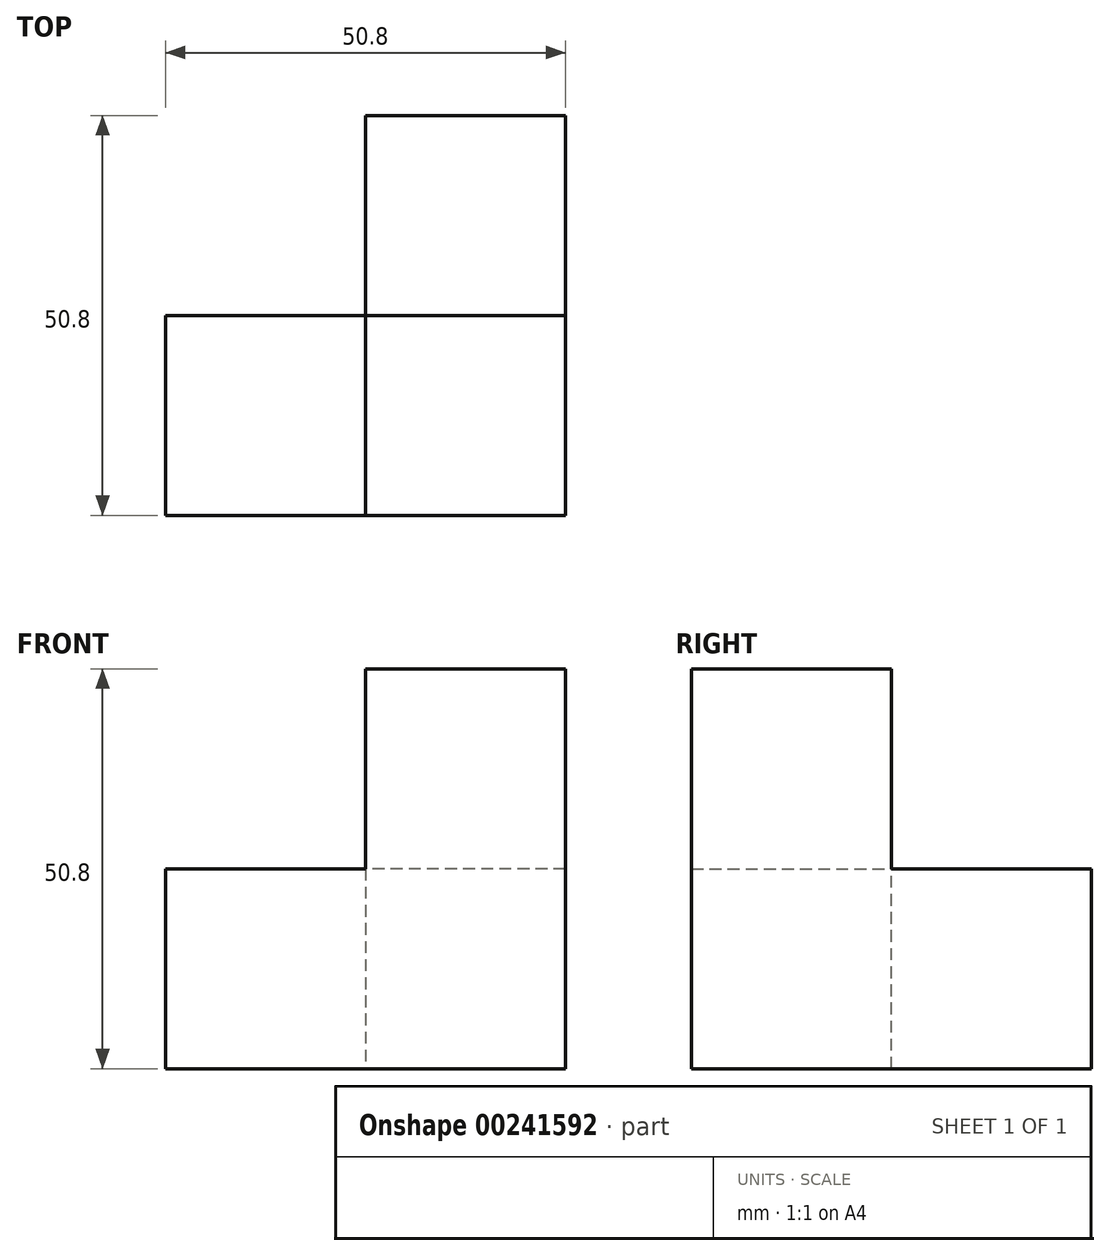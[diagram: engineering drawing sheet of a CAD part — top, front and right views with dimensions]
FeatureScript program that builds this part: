
annotation { "Feature Type Name" : "Feature", "Feature Type Description" : "" }
export const myFeature = defineFeature(function(context is Context, id is Id, definition is map)
    precondition{}
    {
        {
            var Q0;
            Q0=qCreatedBy(makeId("Front.planeOp"),FACE);
            var sketch = newSketch(context, id + "F0", { "sketchPlane" : qUnion([Q0])});
            skLineSegment(sketch, "E0.bottom", {"start": v(0, 0) * mm, "end": v(-25.4, 0) * mm});
            skLineSegment(sketch, "E0.top", {"start": v(0, 25.4) * mm, "end": v(-25.4, 25.4) * mm});
            skLineSegment(sketch, "E0.left", {"start": v(0, 0) * mm, "end": v(0, 25.4) * mm});
            skLineSegment(sketch, "E0.right", {"start": v(-25.4, 0) * mm, "end": v(-25.4, 25.4) * mm});
            skSolve(sketch);
        }
        {
            var Q0;
            Q0=makeQuery(id+"F0.imprint","IMPRINT",FACE,{"disambiguationData":[TD([[makeQuery(id+"F0.imprint","IMPRINT",EDGE,{"derivedFrom":sQuery(id+"F0.wireOp",EDGE,"E0.bottom")}),-1.0]])]});
            extrude(context, id + "F1", {"entities" : qUnion([Q0]), "depth" : 25.4 * mm});
        }
        {
            var Q0;
            Q0=makeQuery(id+"F1.opExtrude","SWEPT_FACE",FACE,{"disambiguationData":[OSD([sQuery(id+"F0.wireOp",EDGE,"E0.left")])]});
            var sketch = newSketch(context, id + "F2", { "sketchPlane" : qUnion([Q0])});
            skLineSegment(sketch, "E1.bottom", {"start": v(-25.4, 25.4) * mm, "end": v(0, 25.4) * mm});
            skLineSegment(sketch, "E1.top", {"start": v(-25.4, 0) * mm, "end": v(0, 0) * mm});
            skLineSegment(sketch, "E1.left", {"start": v(-25.4, 25.4) * mm, "end": v(-25.4, 0) * mm});
            skLineSegment(sketch, "E1.right", {"start": v(0, 25.4) * mm, "end": v(0, 0) * mm});
            skSolve(sketch);
        }
        {
            var Q0;
            Q0=makeQuery(id+"F2.imprint","IMPRINT",FACE,{"disambiguationData":[TD([[makeQuery(id+"F2.imprint","IMPRINT",EDGE,{"derivedFrom":sQuery(id+"F2.wireOp",EDGE,"E1.bottom")}),-1.0]])]});
            extrude(context, id + "F3", {"entities" : qUnion([Q0]), "operationType" : NewBodyOperationType.ADD, "depth" : 25.4 * mm});
        }
        {
            var Q0;
            Q0=makeQuery(id+"F3.boolean.opBoolean","MERGE",FACE,{"derivedFrom":[makeQuery(id+"F1.opExtrude","CAP_FACE",FACE,{"disambiguationData":[OSD([sQuery(id+"F0.wireOp",EDGE,"E0.bottom"),sQuery(id+"F0.wireOp",EDGE,"E0.top"),sQuery(id+"F0.wireOp",EDGE,"E0.left"),sQuery(id+"F0.wireOp",EDGE,"E0.right")])],"isStart":true}),makeQuery(id+"F3.opExtrude","SWEPT_FACE",FACE,{"disambiguationData":[OSD([sQuery(id+"F2.wireOp",EDGE,"E1.right")])]})]});
            var sketch = newSketch(context, id + "F4", { "sketchPlane" : qUnion([Q0])});
            skLineSegment(sketch, "E2.bottom", {"start": v(-25.4, 25.4) * mm, "end": v(0, 25.4) * mm});
            skLineSegment(sketch, "E2.top", {"start": v(-25.4, 0) * mm, "end": v(0, 0) * mm});
            skLineSegment(sketch, "E2.left", {"start": v(-25.4, 25.4) * mm, "end": v(-25.4, 0) * mm});
            skLineSegment(sketch, "E2.right", {"start": v(0, 25.4) * mm, "end": v(0, 0) * mm});
            skSolve(sketch);
        }
        {
            var Q0;
            Q0=makeQuery(id+"F4.imprint","IMPRINT",FACE,{"disambiguationData":[TD([[makeQuery(id+"F4.imprint","IMPRINT",EDGE,{"derivedFrom":sQuery(id+"F4.wireOp",EDGE,"E2.bottom")}),-1.0]])]});
            extrude(context, id + "F5", {"entities" : qUnion([Q0]), "operationType" : NewBodyOperationType.ADD, "depth" : 25.4 * mm});
        }
        {
            var Q0;
            Q0=makeQuery(id+"F5.boolean.opBoolean","MERGE",FACE,{"derivedFrom":[makeQuery(id+"F3.boolean.opBoolean","MERGE",FACE,{"derivedFrom":[makeQuery(id+"F1.opExtrude","SWEPT_FACE",FACE,{"disambiguationData":[OSD([sQuery(id+"F0.wireOp",EDGE,"E0.top")])]}),makeQuery(id+"F3.opExtrude","SWEPT_FACE",FACE,{"disambiguationData":[OSD([sQuery(id+"F2.wireOp",EDGE,"E1.bottom")])]})]}),makeQuery(id+"F5.opExtrude","SWEPT_FACE",FACE,{"disambiguationData":[OSD([sQuery(id+"F4.wireOp",EDGE,"E2.bottom")])]})]});
            var sketch = newSketch(context, id + "F6", { "sketchPlane" : qUnion([Q0])});
            skLineSegment(sketch, "E3.bottom", {"start": v(25.4, -25.4) * mm, "end": v(0, -25.4) * mm});
            skLineSegment(sketch, "E3.top", {"start": v(25.4, 0) * mm, "end": v(0, 0) * mm});
            skLineSegment(sketch, "E3.left", {"start": v(25.4, -25.4) * mm, "end": v(25.4, 0) * mm});
            skLineSegment(sketch, "E3.right", {"start": v(0, -25.4) * mm, "end": v(0, 0) * mm});
            skSolve(sketch);
        }
        {
            var Q0;
            Q0=makeQuery(id+"F6.imprint","IMPRINT",FACE,{"disambiguationData":[TD([[makeQuery(id+"F6.imprint","IMPRINT",EDGE,{"derivedFrom":sQuery(id+"F6.wireOp",EDGE,"E3.bottom")}),-1.0]])]});
            extrude(context, id + "F7", {"entities" : qUnion([Q0]), "operationType" : NewBodyOperationType.ADD, "depth" : 25.4 * mm});
        }
    });
